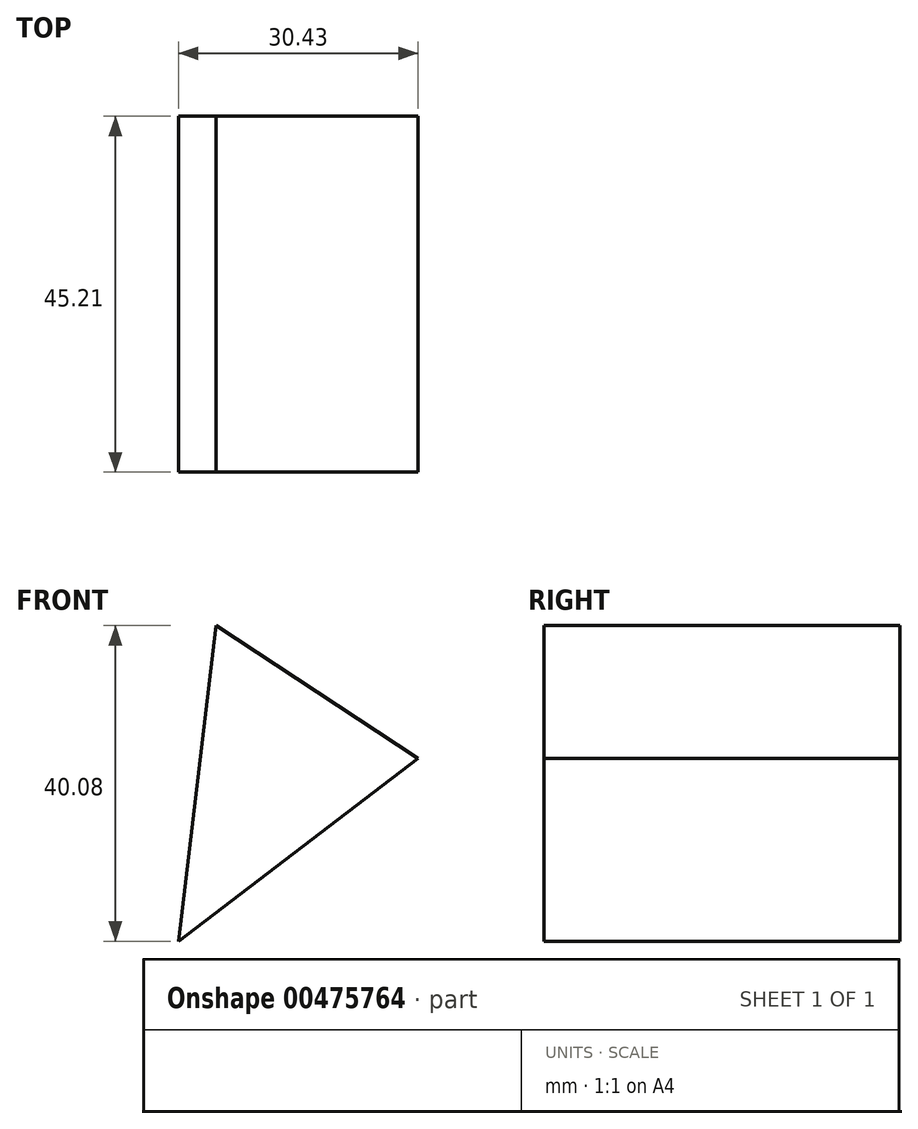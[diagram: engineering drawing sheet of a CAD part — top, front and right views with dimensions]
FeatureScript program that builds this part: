
annotation { "Feature Type Name" : "Feature", "Feature Type Description" : "" }
export const myFeature = defineFeature(function(context is Context, id is Id, definition is map)
    precondition{}
    {
        {
            var Q0;
            Q0=qCreatedBy(makeId("Front.planeOp"),FACE);
            var sketch = newSketch(context, id + "F0", { "sketchPlane" : qUnion([Q0])});
            skLineSegment(sketch, "E0", {"start": v(-34.96, 18.53) * mm, "end": v(-60.57, 35.4) * mm});
            skLineSegment(sketch, "E1", {"start": v(-60.57, 35.4) * mm, "end": v(-65.4, -4.67) * mm});
            skLineSegment(sketch, "E2", {"start": v(-65.4, -4.67) * mm, "end": v(-34.96, 18.53) * mm});
            skSolve(sketch);
        }
        {
            var Q0;
            Q0 = qSketchRegion(id + "F0", true);
            extrude(context, id + "F1", {"entities" : qUnion([Q0]), "depth" : 45.2 * mm});
        }
    });
